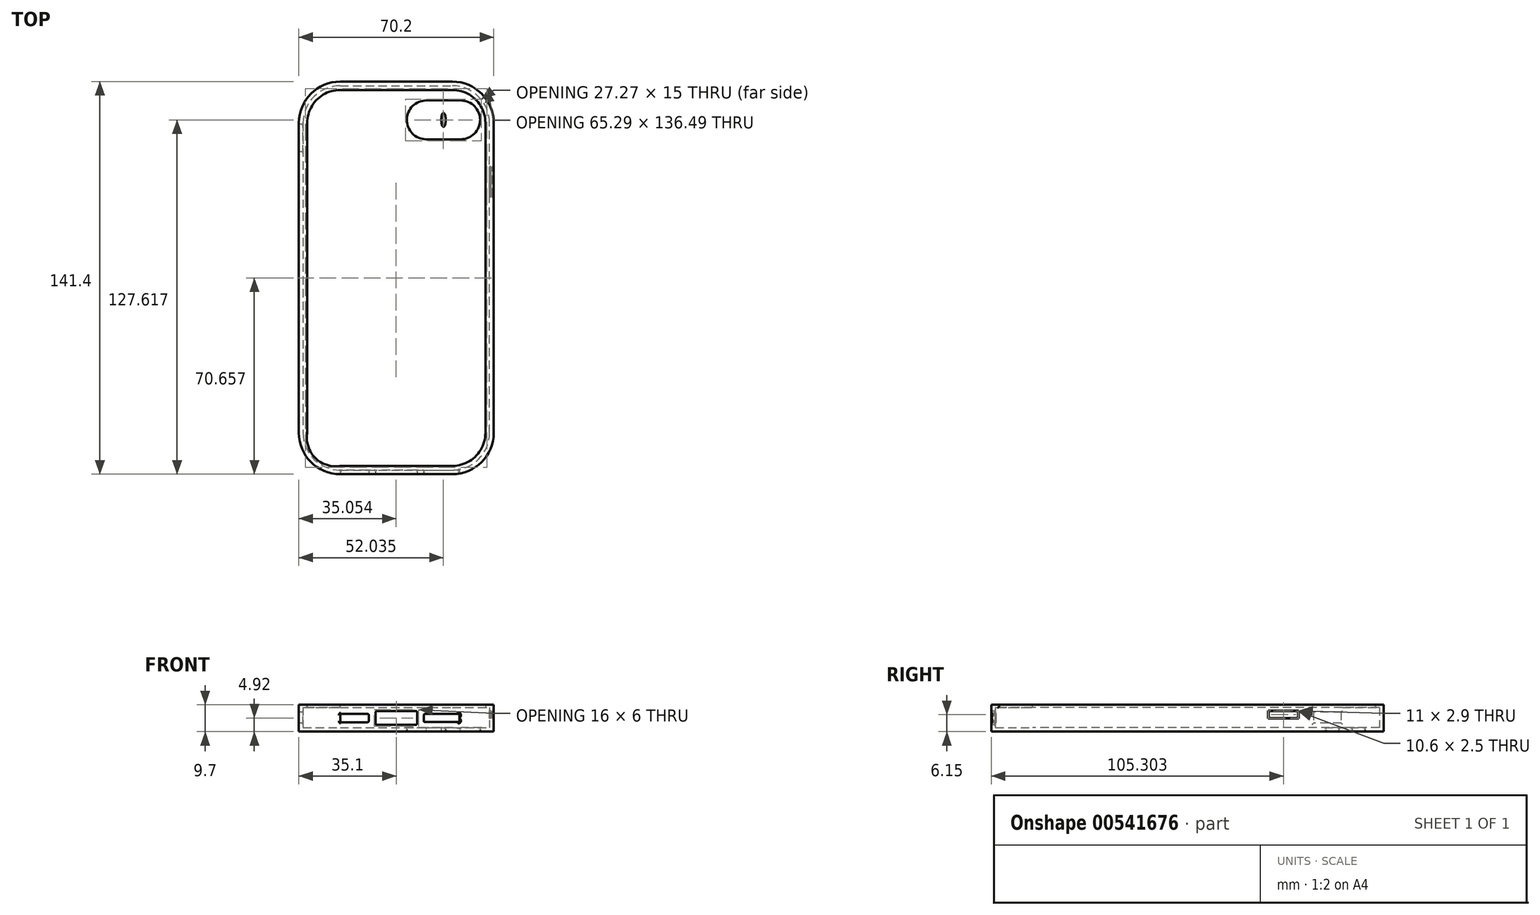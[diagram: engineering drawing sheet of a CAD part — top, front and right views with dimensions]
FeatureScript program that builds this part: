
annotation { "Feature Type Name" : "Feature", "Feature Type Description" : "" }
export const myFeature = defineFeature(function(context is Context, id is Id, definition is map)
    precondition{}
    {
        {
            var Q0;
            Q0=qCreatedBy(makeId("Top.planeOp"),FACE);
            var sketch = newSketch(context, id + "F0", { "sketchPlane" : qUnion([Q0])});
            skArc(sketch, "E0", {"start": v(-23.7, 70.7) * mm, "mid": v(-33.18, 66.77) * mm, "end": v(-37.1, 57.3) * mm});
            skArc(sketch, "E1", {"start": v(-37.1, -54.3) * mm, "mid": v(-33.18, -63.78) * mm, "end": v(-23.7, -67.7) * mm});
            skArc(sketch, "E2", {"start": v(16.7, -67.7) * mm, "mid": v(26.18, -63.78) * mm, "end": v(30.1, -54.3) * mm});
            skArc(sketch, "E3", {"start": v(30.1, 57.3) * mm, "mid": v(26.18, 66.77) * mm, "end": v(16.7, 70.7) * mm});
            skLineSegment(sketch, "E4", {"start": v(-23.7, -67.7) * mm, "end": v(16.7, -67.7) * mm});
            skLineSegment(sketch, "E5", {"start": v(30.1, -54.3) * mm, "end": v(30.1, 57.3) * mm});
            skLineSegment(sketch, "E6", {"start": v(-37.1, 57.3) * mm, "end": v(-37.1, -54.3) * mm});
            skLineSegment(sketch, "E7", {"start": v(-23.7, 70.7) * mm, "end": v(16.7, 70.7) * mm});
            skLineSegment(sketch, "E8.0", {"start": v(-23.7, 72.2) * mm, "end": v(16.7, 72.2) * mm});
            skArc(sketch, "E8.1", {"start": v(31.6, 57.3) * mm, "mid": v(27.24, 67.83) * mm, "end": v(16.7, 72.2) * mm});
            skArc(sketch, "E8.2", {"start": v(-23.7, 72.2) * mm, "mid": v(-34.24, 67.83) * mm, "end": v(-38.6, 57.3) * mm});
            skLineSegment(sketch, "E8.3", {"start": v(31.6, -54.3) * mm, "end": v(31.6, 57.3) * mm});
            skLineSegment(sketch, "E8.4", {"start": v(-38.6, 57.3) * mm, "end": v(-38.6, -54.3) * mm});
            skArc(sketch, "E8.5", {"start": v(-38.6, -54.3) * mm, "mid": v(-34.24, -64.84) * mm, "end": v(-23.7, -69.2) * mm});
            skLineSegment(sketch, "E8.6", {"start": v(-23.7, -69.2) * mm, "end": v(16.7, -69.2) * mm});
            skArc(sketch, "E8.7", {"start": v(16.7, -69.2) * mm, "mid": v(27.24, -64.84) * mm, "end": v(31.6, -54.3) * mm});
            skLineSegment(sketch, "E9", {"start": v(-37.1, -54.3) * mm, "end": v(-3.5, -54.3) * mm, "construction": true});
            skLineSegment(sketch, "E10", {"start": v(-3.5, -54.3) * mm, "end": v(-3.5, -67.7) * mm, "construction": true});
            skSolve(sketch);
        }
        {
            var Q0;
            Q0=makeQuery(id+"F0.imprint","IMPRINT",FACE,{"disambiguationData":[TD([[makeQuery(id+"F0.imprint","IMPRINT",EDGE,{"derivedFrom":sQuery(id+"F0.wireOp",EDGE,"E0")}),-1.0]])]});
            extrude(context, id + "F1", {"entities" : qUnion([Q0]), "depth" : 8.2 * mm, "offsetDistance" : 25 * mm});
        }
        {
            var Q0;
            Q0=makeQuery(id+"F0.imprint","IMPRINT",FACE,{"disambiguationData":[TD([[makeQuery(id+"F0.imprint","IMPRINT",EDGE,{"derivedFrom":sQuery(id+"F0.wireOp",EDGE,"E0")}),1.0]])]});
            var Q1;
            Q1=makeQuery(id+"F0.imprint","IMPRINT",FACE,{"disambiguationData":[TD([[makeQuery(id+"F0.imprint","IMPRINT",EDGE,{"derivedFrom":sQuery(id+"F0.wireOp",EDGE,"E0")}),-1.0]])]});
            extrude(context, id + "F2", {"entities" : qUnion([Q0, Q1]), "operationType" : NewBodyOperationType.ADD, "oppositeDirection" : true, "depth" : 1.5 * mm, "offsetDistance" : 25 * mm});
        }
        {
            var Q0;
            {var subQ0=sQuery(id+"F0.wireOp",EDGE,"E8.6");Q0=makeQuery(id+"F2.boolean.opBoolean","MERGE",FACE,{"derivedFrom":[makeQuery(id+"F1.opExtrude","SWEPT_FACE",FACE,{"disambiguationData":[OSD([subQ0])]}),makeQuery(id+"F2.opExtrude","SWEPT_FACE",FACE,{"disambiguationData":[OSD([subQ0])]})]});}
            var sketch = newSketch(context, id + "F3", { "sketchPlane" : qUnion([Q0])});
            skLineSegment(sketch, "E11", {"start": v(-23.7, 3.42) * mm, "end": v(16.7, 3.42) * mm, "construction": true});
            skLineSegment(sketch, "E12", {"start": v(-3.5, -1.5) * mm, "end": v(-3.5, 8.2) * mm, "construction": true});
            skLineSegment(sketch, "E13.bottom", {"start": v(-11, 5.92) * mm, "end": v(4, 5.92) * mm});
            skLineSegment(sketch, "E13.top", {"start": v(-11, 0.92) * mm, "end": v(4, 0.92) * mm});
            skLineSegment(sketch, "E13.left", {"start": v(-11, 5.92) * mm, "end": v(-11, 0.92) * mm});
            skLineSegment(sketch, "E13.right", {"start": v(4, 5.92) * mm, "end": v(4, 0.92) * mm});
            skPoint(sketch, "E13.middle", {"position": v(-3.5, 3.42) * mm});
            skLineSegment(sketch, "E14.bottom", {"start": v(-23.7, 3.42) * mm, "end": v(-10.9, 3.42) * mm});
            skLineSegment(sketch, "E14.top", {"start": v(-26.2, 4.92) * mm, "end": v(-13.4, 4.92) * mm});
            skLineSegment(sketch, "E14.left", {"start": v(-26.2, 3.42) * mm, "end": v(-26.2, 4.92) * mm});
            skLineSegment(sketch, "E14.right", {"start": v(-13.4, 3.42) * mm, "end": v(-13.4, 4.92) * mm});
            skLineSegment(sketch, "E15.top", {"start": v(-26.2, 1.87) * mm, "end": v(-13.4, 1.87) * mm});
            skLineSegment(sketch, "E15.left", {"start": v(-26.2, 3.42) * mm, "end": v(-26.2, 1.87) * mm});
            skLineSegment(sketch, "E15.right", {"start": v(-13.4, 3.42) * mm, "end": v(-13.4, 1.87) * mm});
            skLineSegment(sketch, "E16.bottom", {"start": v(19.2, 3.42) * mm, "end": v(6.4, 3.42) * mm});
            skLineSegment(sketch, "E16.top", {"start": v(19.2, 4.92) * mm, "end": v(6.4, 4.92) * mm});
            skLineSegment(sketch, "E16.left", {"start": v(19.2, 3.42) * mm, "end": v(19.2, 4.92) * mm});
            skLineSegment(sketch, "E16.right", {"start": v(6.4, 3.42) * mm, "end": v(6.4, 4.92) * mm});
            skLineSegment(sketch, "E17.top", {"start": v(19.2, 1.92) * mm, "end": v(6.4, 1.92) * mm});
            skLineSegment(sketch, "E17.left", {"start": v(19.2, 3.42) * mm, "end": v(19.2, 1.92) * mm});
            skLineSegment(sketch, "E17.right", {"start": v(6.4, 3.42) * mm, "end": v(6.4, 1.92) * mm});
            skSolve(sketch);
        }
        {
            var Q0;
            Q0=makeQuery(id+"F3.imprint","IMPRINT",FACE,{"disambiguationData":[TD([[makeQuery(id+"F3.imprint","IMPRINT",EDGE,{"derivedFrom":sQuery(id+"F3.wireOp",EDGE,"E14.bottom")}),-1.0]])]});
            var Q1;
            Q1=makeQuery(id+"F3.imprint","IMPRINT",FACE,{"disambiguationData":[TD([[makeQuery(id+"F3.imprint","IMPRINT",EDGE,{"derivedFrom":sQuery(id+"F3.wireOp",EDGE,"E14.top")}),-1.0]])]});
            var Q2;
            Q2=makeQuery(id+"F3.imprint","IMPRINT",FACE,{"disambiguationData":[TD([[makeQuery(id+"F3.imprint","IMPRINT",EDGE,{"derivedFrom":sQuery(id+"F3.wireOp",EDGE,"E13.bottom")}),-1.0]])]});
            var Q3;
            Q3=makeQuery(id+"F3.imprint","IMPRINT",FACE,{"disambiguationData":[TD([[makeQuery(id+"F3.imprint","IMPRINT",EDGE,{"derivedFrom":sQuery(id+"F3.wireOp",EDGE,"E16.top")}),1.0]])]});
            var Q4;
            Q4=makeQuery(id+"F3.imprint","IMPRINT",FACE,{"disambiguationData":[TD([[makeQuery(id+"F3.imprint","IMPRINT",EDGE,{"derivedFrom":sQuery(id+"F3.wireOp",EDGE,"E16.bottom")}),1.0]])]});
            extrude(context, id + "F4", {"entities" : qUnion([Q0, Q1, Q2, Q3, Q4]), "operationType" : NewBodyOperationType.REMOVE, "oppositeDirection" : true, "depth" : 3 * mm, "offsetDistance" : 25 * mm});
        }
        {
            var Q0;
            Q0=makeQuery(id+"F2.opExtrude","CAP_FACE",FACE,{"disambiguationData":[OSD([sQuery(id+"F0.wireOp",EDGE,"E8.0"),sQuery(id+"F0.wireOp",EDGE,"E8.1"),sQuery(id+"F0.wireOp",EDGE,"E8.2"),sQuery(id+"F0.wireOp",EDGE,"E8.3"),sQuery(id+"F0.wireOp",EDGE,"E8.4"),sQuery(id+"F0.wireOp",EDGE,"E8.5"),sQuery(id+"F0.wireOp",EDGE,"E8.6"),sQuery(id+"F0.wireOp",EDGE,"E8.7")])],"isStart":false});
            var sketch = newSketch(context, id + "F5", { "sketchPlane" : qUnion([Q0])});
            skCircle(sketch, "E18", {"center": v(19.7, -58.4) * mm, "radius": 7 * mm});
            skCircle(sketch, "E19.1.0.0", {"center": v(7.3, -58.4) * mm, "radius": 7 * mm});
            skLineSegment(sketch, "E19.direction1", {"start": v(19.7, -58.4) * mm, "end": v(7.3, -58.4) * mm, "construction": true});
            skLineSegment(sketch, "E20", {"start": v(19.75, -65.4) * mm, "end": v(7.3, -65.4) * mm});
            skLineSegment(sketch, "E21", {"start": v(7.2, -51.4) * mm, "end": v(19.7, -51.4) * mm});
            skSolve(sketch);
        }
        {
            var Q0;
            {var subQ0=sQuery(id+"F5.wireOp",EDGE,"E18");var subQ3=makeQuery(id+"F5.imprint","IMPRINT",VERTEX,{"derivedFrom":subQ0});Q0=makeQuery(id+"F5.imprint","IMPRINT",FACE,{"disambiguationData":[TD([[makeQuery(id+"F5.imprint","IMPRINT",EDGE,{"disambiguationData":[TD([[subQ3,1.0]])],"derivedFrom":subQ0}),1.0]])]});}
            var Q1;
            {var subQ0=sQuery(id+"F5.wireOp",EDGE,"E19.1.0.0");var subQ1=makeQuery(id+"F5.imprint","INTERSECT",VERTEX,{"derivedFrom":[subQ0,sQuery(id+"F5.wireOp",EDGE,"E20")]});Q1=makeQuery(id+"F5.imprint","IMPRINT",FACE,{"disambiguationData":[TD([[makeQuery(id+"F5.imprint","IMPRINT",EDGE,{"disambiguationData":[TD([[subQ1,1.0]])],"derivedFrom":subQ0}),1.0]])]});}
            var Q2;
            {var subQ0=sQuery(id+"F5.wireOp",EDGE,"E20");Q2=makeQuery(id+"F5.imprint","IMPRINT",FACE,{"disambiguationData":[TD([[makeQuery(id+"F5.imprint","IMPRINT",EDGE,{"derivedFrom":subQ0}),-1.0]])]});}
            var Q3;
            {var subQ0=sQuery(id+"F5.wireOp",EDGE,"E19.1.0.0");var subQ1=sQuery(id+"F5.wireOp",EDGE,"E18");var subQ2=makeQuery(id+"F5.imprint","INTERSECT",VERTEX,{"disambiguationData":[OD(0.0)],"derivedFrom":[subQ1,subQ0]});Q3=makeQuery(id+"F5.imprint","IMPRINT",FACE,{"disambiguationData":[TD([[makeQuery(id+"F5.imprint","IMPRINT",EDGE,{"disambiguationData":[TD([[subQ2,-1.0]])],"derivedFrom":subQ1}),1.0]])]});}
            var Q4;
            {var subQ0=sQuery(id+"F5.wireOp",EDGE,"E21");var subQ1=sQuery(id+"F5.wireOp",EDGE,"E18");var subQ2=makeQuery(id+"F5.imprint","INTERSECT",VERTEX,{"derivedFrom":[subQ1,subQ0]});Q4=makeQuery(id+"F5.imprint","IMPRINT",FACE,{"disambiguationData":[TD([[makeQuery(id+"F5.imprint","IMPRINT",EDGE,{"disambiguationData":[TD([[subQ2,-1.0]])],"derivedFrom":subQ1}),-1.0]])]});}
            extrude(context, id + "F6", {"entities" : qUnion([Q0, Q1, Q2, Q3, Q4]), "operationType" : NewBodyOperationType.REMOVE, "oppositeDirection" : true, "depth" : 5 * mm, "offsetDistance" : 25 * mm});
        }
        {
            var Q0;
            Q0=makeQuery(id+"F1.opExtrude","SWEPT_FACE",FACE,{"disambiguationData":[OSD([sQuery(id+"F0.wireOp",EDGE,"E5")])]});
            var sketch = newSketch(context, id + "F7", { "sketchPlane" : qUnion([Q0])});
            skLineSegment(sketch, "E22", {"start": v(-57.3, 4.65) * mm, "end": v(-33.08, 4.65) * mm, "construction": true});
            skLineSegment(sketch, "E23", {"start": v(-36.1, 8.2) * mm, "end": v(-36.1, 0) * mm, "construction": true});
            skLineSegment(sketch, "E24.bottom", {"start": v(-36.1, 4.65) * mm, "end": v(-41.4, 4.65) * mm});
            skLineSegment(sketch, "E24.top", {"start": v(-36.1, 5.9) * mm, "end": v(-41.4, 5.9) * mm});
            skLineSegment(sketch, "E24.left", {"start": v(-36.1, 4.65) * mm, "end": v(-36.1, 5.9) * mm});
            skLineSegment(sketch, "E24.right", {"start": v(-41.4, 4.65) * mm, "end": v(-41.4, 5.9) * mm});
            skLineSegment(sketch, "E25.top", {"start": v(-36.1, 3.4) * mm, "end": v(-41.4, 3.4) * mm});
            skLineSegment(sketch, "E25.left", {"start": v(-36.1, 4.65) * mm, "end": v(-36.1, 3.4) * mm});
            skLineSegment(sketch, "E25.right", {"start": v(-41.4, 4.65) * mm, "end": v(-41.4, 3.4) * mm});
            skLineSegment(sketch, "E26.bottom", {"start": v(-41.4, 5.9) * mm, "end": v(-30.8, 5.9) * mm});
            skLineSegment(sketch, "E26.top", {"start": v(-41.4, 3.4) * mm, "end": v(-30.8, 3.4) * mm});
            skLineSegment(sketch, "E26.right", {"start": v(-30.8, 5.9) * mm, "end": v(-30.8, 3.4) * mm});
            skPoint(sketch, "E26.middle", {"position": v(-36.1, 4.65) * mm});
            skLineSegment(sketch, "E27.0", {"start": v(-41.6, 6.1) * mm, "end": v(-30.6, 6.1) * mm});
            skLineSegment(sketch, "E27.1", {"start": v(-41.6, 4.65) * mm, "end": v(-41.6, 6.1) * mm});
            skLineSegment(sketch, "E27.2", {"start": v(-30.6, 6.1) * mm, "end": v(-30.6, 3.2) * mm});
            skLineSegment(sketch, "E27.3", {"start": v(-41.6, 3.2) * mm, "end": v(-30.6, 3.2) * mm});
            skLineSegment(sketch, "E27.4", {"start": v(-41.6, 4.65) * mm, "end": v(-41.6, 3.2) * mm});
            skSolve(sketch);
        }
        {
            var Q0;
            {var subQ4=sQuery(id+"F7.wireOp",EDGE,"E24.right");Q0=makeQuery(id+"F7.imprint","IMPRINT",FACE,{"disambiguationData":[TD([[makeQuery(id+"F7.imprint","IMPRINT",EDGE,{"derivedFrom":subQ4}),1.0]])]});}
            extrude(context, id + "F8", {"entities" : qUnion([Q0]), "operationType" : NewBodyOperationType.REMOVE, "oppositeDirection" : true, "depth" : .5 * mm, "offsetDistance" : 25 * mm});
        }
        {
            var Q0;
            {var subQ0=sQuery(id+"F0.wireOp",EDGE,"E8.3");Q0=makeQuery(id+"F2.boolean.opBoolean","MERGE",FACE,{"derivedFrom":[makeQuery(id+"F1.opExtrude","SWEPT_FACE",FACE,{"disambiguationData":[OSD([subQ0])]}),makeQuery(id+"F2.opExtrude","SWEPT_FACE",FACE,{"disambiguationData":[OSD([subQ0])]})]});}
            var sketch = newSketch(context, id + "F9", { "sketchPlane" : qUnion([Q0])});
            skLineSegment(sketch, "E28.bottom", {"start": v(30.8, 5.9) * mm, "end": v(41.4, 5.9) * mm});
            skLineSegment(sketch, "E28.top", {"start": v(30.8, 3.4) * mm, "end": v(41.4, 3.4) * mm});
            skLineSegment(sketch, "E28.right", {"start": v(41.4, 5.9) * mm, "end": v(41.4, 3.4) * mm});
            skLineSegment(sketch, "E29", {"start": v(30.8, 5.9) * mm, "end": v(30.8, 3.4) * mm});
            skLineSegment(sketch, "E30.0", {"start": v(41.6, 6.1) * mm, "end": v(41.6, 3.2) * mm});
            skLineSegment(sketch, "E30.1", {"start": v(30.6, 6.1) * mm, "end": v(41.6, 6.1) * mm});
            skLineSegment(sketch, "E30.2", {"start": v(30.6, 6.1) * mm, "end": v(30.6, 3.2) * mm});
            skLineSegment(sketch, "E30.3", {"start": v(30.6, 3.2) * mm, "end": v(41.6, 3.2) * mm});
            skLineSegment(sketch, "E31.0", {"start": v(-59.3, 13.2) * mm, "end": v(-59.3, -6.5) * mm});
            skLineSegment(sketch, "E31.1", {"start": v(62.3, 13.2) * mm, "end": v(-59.3, 13.2) * mm});
            skLineSegment(sketch, "E31.2", {"start": v(62.3, -6.5) * mm, "end": v(62.3, 13.2) * mm});
            skLineSegment(sketch, "E31.3", {"start": v(-59.3, -6.5) * mm, "end": v(62.3, -6.5) * mm});
            skSolve(sketch);
        }
        {
            var Q0;
            Q0=makeQuery(id+"F9.imprint","IMPRINT",FACE,{"disambiguationData":[TD([[makeQuery(id+"F9.imprint","IMPRINT",EDGE,{"derivedFrom":sQuery(id+"F9.wireOp",EDGE,"E28.bottom")}),1.0]])]});
            extrude(context, id + "F10", {"entities" : qUnion([Q0]), "operationType" : NewBodyOperationType.REMOVE, "oppositeDirection" : true, "depth" : .5 * mm, "offsetDistance" : 25 * mm});
        }
        {
            var Q0;
            {var subQ0=sQuery(id+"F0.wireOp",EDGE,"E8.4");Q0=makeQuery(id+"F2.boolean.opBoolean","MERGE",FACE,{"derivedFrom":[makeQuery(id+"F1.opExtrude","SWEPT_FACE",FACE,{"disambiguationData":[OSD([subQ0])]}),makeQuery(id+"F2.opExtrude","SWEPT_FACE",FACE,{"disambiguationData":[OSD([subQ0])]})]});}
            var sketch = newSketch(context, id + "F11", { "sketchPlane" : qUnion([Q0])});
            skLineSegment(sketch, "E32", {"start": v(-68.46, 3.55) * mm, "end": v(5.63, 3.55) * mm, "construction": true});
            skLineSegment(sketch, "E33", {"start": v(-56.9, 8.2) * mm, "end": v(-56.9, 0) * mm, "construction": true});
            skLineSegment(sketch, "E34.bottom", {"start": v(-56.9, 3.55) * mm, "end": v(-46.9, 3.55) * mm});
            skLineSegment(sketch, "E34.top", {"start": v(-56.9, 5.55) * mm, "end": v(-46.9, 5.55) * mm});
            skLineSegment(sketch, "E34.left", {"start": v(-56.9, 3.55) * mm, "end": v(-56.9, 5.55) * mm});
            skLineSegment(sketch, "E34.right", {"start": v(-46.9, 3.55) * mm, "end": v(-46.9, 5.55) * mm});
            skLineSegment(sketch, "E35.top", {"start": v(-56.9, 1.55) * mm, "end": v(-46.9, 1.55) * mm});
            skLineSegment(sketch, "E35.left", {"start": v(-56.9, 5.55) * mm, "end": v(-56.9, 1.55) * mm});
            skLineSegment(sketch, "E35.right", {"start": v(-46.9, 5.55) * mm, "end": v(-46.9, 1.55) * mm});
            skSolve(sketch);
        }
        {
            var Q0;
            {var subQ0=sQuery(id+"F11.wireOp",EDGE,"E34.bottom");Q0=makeQuery(id+"F11.imprint","IMPRINT",FACE,{"disambiguationData":[TD([[makeQuery(id+"F11.imprint","IMPRINT",EDGE,{"derivedFrom":subQ0}),-1.0]])]});}
            var Q1;
            {var subQ0=sQuery(id+"F11.wireOp",EDGE,"E34.bottom");Q1=makeQuery(id+"F11.imprint","IMPRINT",FACE,{"disambiguationData":[TD([[makeQuery(id+"F11.imprint","IMPRINT",EDGE,{"derivedFrom":subQ0}),1.0]])]});}
            extrude(context, id + "F12", {"entities" : qUnion([Q0, Q1]), "operationType" : NewBodyOperationType.REMOVE, "oppositeDirection" : true, "depth" : 5 * mm, "offsetDistance" : 25 * mm});
        }
        {
            var Q0;
            Q0=makeQuery(id+"F1.opExtrude","CAP_FACE",FACE,{"disambiguationData":[OSD([sQuery(id+"F0.wireOp",EDGE,"E0"),sQuery(id+"F0.wireOp",EDGE,"E1"),sQuery(id+"F0.wireOp",EDGE,"E2"),sQuery(id+"F0.wireOp",EDGE,"E3"),sQuery(id+"F0.wireOp",EDGE,"E4"),sQuery(id+"F0.wireOp",EDGE,"E5"),sQuery(id+"F0.wireOp",EDGE,"E6"),sQuery(id+"F0.wireOp",EDGE,"E7"),sQuery(id+"F0.wireOp",EDGE,"E8.0"),sQuery(id+"F0.wireOp",EDGE,"E8.1"),sQuery(id+"F0.wireOp",EDGE,"E8.2"),sQuery(id+"F0.wireOp",EDGE,"E8.3"),sQuery(id+"F0.wireOp",EDGE,"E8.4"),sQuery(id+"F0.wireOp",EDGE,"E8.5"),sQuery(id+"F0.wireOp",EDGE,"E8.6"),sQuery(id+"F0.wireOp",EDGE,"E8.7")])],"isStart":false});
            var sketch = newSketch(context, id + "F13", { "sketchPlane" : qUnion([Q0])});
            skArc(sketch, "E36", {"start": v(-23.7, 70.7) * mm, "mid": v(-33.18, 66.77) * mm, "end": v(-37.1, 57.3) * mm});
            skArc(sketch, "E37", {"start": v(-37.1, -54.3) * mm, "mid": v(-33.77, -64.38) * mm, "end": v(-23.7, -67.7) * mm});
            skArc(sketch, "E38", {"start": v(16.7, -67.7) * mm, "mid": v(26.18, -63.78) * mm, "end": v(30.1, -54.3) * mm});
            skArc(sketch, "E39", {"start": v(30.1, 57.3) * mm, "mid": v(26.18, 66.77) * mm, "end": v(16.7, 70.7) * mm});
            skLineSegment(sketch, "E40", {"start": v(-23.7, -67.7) * mm, "end": v(16.7, -67.7) * mm});
            skLineSegment(sketch, "E41", {"start": v(30.1, -54.3) * mm, "end": v(30.1, 57.3) * mm});
            skLineSegment(sketch, "E42", {"start": v(-37.1, 57.3) * mm, "end": v(-37.1, -54.3) * mm});
            skLineSegment(sketch, "E43", {"start": v(-23.7, 70.7) * mm, "end": v(16.7, 70.7) * mm});
            skLineSegment(sketch, "E44", {"start": v(-37.1, -54.3) * mm, "end": v(-3.5, -54.3) * mm, "construction": true});
            skLineSegment(sketch, "E45", {"start": v(-3.5, -54.3) * mm, "end": v(-3.5, -67.7) * mm, "construction": true});
            skArc(sketch, "E46.0", {"start": v(16.7, -66.2) * mm, "mid": v(25.11, -62.72) * mm, "end": v(28.6, -54.3) * mm});
            skLineSegment(sketch, "E46.1", {"start": v(-23.81, -66.2) * mm, "end": v(16.7, -66.2) * mm});
            skLineSegment(sketch, "E46.2", {"start": v(28.6, -54.3) * mm, "end": v(28.6, 57.3) * mm});
            skArc(sketch, "E46.3", {"start": v(-35.6, -54.42) * mm, "mid": v(-32.71, -63.32) * mm, "end": v(-23.81, -66.2) * mm});
            skArc(sketch, "E46.4", {"start": v(28.6, 57.3) * mm, "mid": v(25.11, 65.7) * mm, "end": v(16.7, 69.2) * mm});
            skLineSegment(sketch, "E46.5", {"start": v(-23.7, 69.2) * mm, "end": v(16.7, 69.2) * mm});
            skArc(sketch, "E46.6", {"start": v(-23.7, 69.2) * mm, "mid": v(-32.11, 65.7) * mm, "end": v(-35.6, 57.3) * mm});
            skLineSegment(sketch, "E46.7", {"start": v(-35.6, 57.3) * mm, "end": v(-35.6, -54.42) * mm});
            skSolve(sketch);
        }
        {
            var Q0;
            Q0=makeQuery(id+"F13.imprint","IMPRINT",FACE,{"disambiguationData":[TD([[makeQuery(id+"F13.imprint","IMPRINT",EDGE,{"derivedFrom":sQuery(id+"F13.wireOp",EDGE,"E36")}),1.0]])]});
            extrude(context, id + "F14", {"entities" : qUnion([Q0]), "operationType" : NewBodyOperationType.ADD, "oppositeDirection" : true, "depth" : 1 * mm, "offsetDistance" : 25 * mm});
        }
        {
            var Q0;
            Q0=makeQuery(id+"F14.opExtrude","CAP_EDGE",EDGE,{"disambiguationData":[OSD([sQuery(id+"F13.wireOp",EDGE,"E46.7")])],"isStart":true});
            var Q1;
            Q1=makeQuery(id+"F14.opExtrude","CAP_EDGE",EDGE,{"disambiguationData":[OSD([sQuery(id+"F13.wireOp",EDGE,"E46.7")])],"isStart":false});
            var Q2;
            Q2=makeQuery(id+"F14.opExtrude","CAP_EDGE",EDGE,{"disambiguationData":[OSD([sQuery(id+"F13.wireOp",EDGE,"E46.3")])],"isStart":true});
            var Q3;
            Q3=makeQuery(id+"F14.opExtrude","CAP_EDGE",EDGE,{"disambiguationData":[OSD([sQuery(id+"F13.wireOp",EDGE,"E46.3")])],"isStart":false});
            var Q4;
            Q4=makeQuery(id+"F6.boolean.opBoolean","COPY",FACE,{"derivedFrom":makeQuery(id+"F6.opExtrude","SWEPT_FACE",FACE,{"disambiguationData":[OSD([sQuery(id+"F5.wireOp",EDGE,"E19.1.0.0")])]})});
            var Q5;
            Q5=makeQuery(id+"F12.boolean.opBoolean","COPY",EDGE,{"derivedFrom":makeQuery(id+"F12.opExtrude","CAP_EDGE",EDGE,{"disambiguationData":[OSD([sQuery(id+"F11.wireOp",EDGE,"E35.top")])],"isStart":true})});
            var Q6;
            Q6=makeQuery(id+"F12.boolean.opBoolean","INTERSECT",EDGE,{"derivedFrom":[makeQuery(id+"F1.opExtrude","SWEPT_FACE",FACE,{"disambiguationData":[OSD([sQuery(id+"F0.wireOp",EDGE,"E6")])]}),makeQuery(id+"F12.opExtrude","SWEPT_FACE",FACE,{"disambiguationData":[OSD([sQuery(id+"F11.wireOp",EDGE,"E35.top")])]})]});
            var Q7;
            Q7=makeQuery(id+"F12.boolean.opBoolean","COPY",EDGE,{"derivedFrom":makeQuery(id+"F12.opExtrude","CAP_EDGE",EDGE,{"disambiguationData":[OSD([sQuery(id+"F11.wireOp",EDGE,"E35.right")])],"isStart":true})});
            var Q8;
            Q8=makeQuery(id+"F12.boolean.opBoolean","INTERSECT",EDGE,{"derivedFrom":[makeQuery(id+"F1.opExtrude","SWEPT_FACE",FACE,{"disambiguationData":[OSD([sQuery(id+"F0.wireOp",EDGE,"E6")])]}),makeQuery(id+"F12.opExtrude","SWEPT_FACE",FACE,{"disambiguationData":[OSD([sQuery(id+"F11.wireOp",EDGE,"E35.right")])]})]});
            var Q9;
            Q9=makeQuery(id+"F12.boolean.opBoolean","INTERSECT",EDGE,{"derivedFrom":[makeQuery(id+"F1.opExtrude","SWEPT_FACE",FACE,{"disambiguationData":[OSD([sQuery(id+"F0.wireOp",EDGE,"E6")])]}),makeQuery(id+"F12.opExtrude","SWEPT_FACE",FACE,{"disambiguationData":[OSD([sQuery(id+"F11.wireOp",EDGE,"E35.left")])]})]});
            var Q10;
            Q10=makeQuery(id+"F12.boolean.opBoolean","COPY",EDGE,{"derivedFrom":makeQuery(id+"F12.opExtrude","CAP_EDGE",EDGE,{"disambiguationData":[OSD([sQuery(id+"F11.wireOp",EDGE,"E35.left")])],"isStart":true})});
            var Q11;
            Q11=makeQuery(id+"F12.boolean.opBoolean","INTERSECT",EDGE,{"derivedFrom":[makeQuery(id+"F1.opExtrude","SWEPT_FACE",FACE,{"disambiguationData":[OSD([sQuery(id+"F0.wireOp",EDGE,"E6")])]}),makeQuery(id+"F12.opExtrude","SWEPT_FACE",FACE,{"disambiguationData":[OSD([sQuery(id+"F11.wireOp",EDGE,"E34.top")])]})]});
            var Q12;
            Q12=makeQuery(id+"F12.boolean.opBoolean","COPY",EDGE,{"derivedFrom":makeQuery(id+"F12.opExtrude","CAP_EDGE",EDGE,{"disambiguationData":[OSD([sQuery(id+"F11.wireOp",EDGE,"E34.top")])],"isStart":true})});
            var Q13;
            Q13=makeQuery(id+"F4.boolean.opBoolean","COPY",FACE,{"derivedFrom":makeQuery(id+"F4.opExtrude","SWEPT_FACE",FACE,{"disambiguationData":[OSD([sQuery(id+"F3.wireOp",EDGE,"E13.top")])]})});
            var Q14;
            Q14=makeQuery(id+"F4.boolean.opBoolean","COPY",FACE,{"derivedFrom":makeQuery(id+"F4.opExtrude","SWEPT_FACE",FACE,{"disambiguationData":[OSD([sQuery(id+"F3.wireOp",EDGE,"E13.bottom")])]})});
            var Q15;
            Q15=makeQuery(id+"F4.boolean.opBoolean","COPY",FACE,{"derivedFrom":makeQuery(id+"F4.opExtrude","SWEPT_FACE",FACE,{"disambiguationData":[OSD([sQuery(id+"F0.wireOp",EDGE,"E8.5"),sQuery(id+"F0.wireOp",EDGE,"E8.6")])]})});
            var Q16;
            Q16=makeQuery(id+"F4.boolean.opBoolean","COPY",FACE,{"derivedFrom":makeQuery(id+"F4.opExtrude","SWEPT_FACE",FACE,{"disambiguationData":[OSD([sQuery(id+"F3.wireOp",EDGE,"E14.top")])]})});
            var Q17;
            Q17=makeQuery(id+"F4.boolean.opBoolean","COPY",FACE,{"derivedFrom":makeQuery(id+"F4.opExtrude","SWEPT_FACE",FACE,{"disambiguationData":[OSD([sQuery(id+"F3.wireOp",EDGE,"E14.right"),sQuery(id+"F3.wireOp",EDGE,"E15.right")])]})});
            var Q18;
            Q18=makeQuery(id+"F4.boolean.opBoolean","COPY",FACE,{"derivedFrom":makeQuery(id+"F4.opExtrude","SWEPT_FACE",FACE,{"disambiguationData":[OSD([sQuery(id+"F3.wireOp",EDGE,"E15.top")])]})});
            var Q19;
            Q19=makeQuery(id+"F4.boolean.opBoolean","COPY",FACE,{"derivedFrom":makeQuery(id+"F4.opExtrude","SWEPT_FACE",FACE,{"disambiguationData":[OSD([sQuery(id+"F3.wireOp",EDGE,"E17.top")])]})});
            var Q20;
            Q20=makeQuery(id+"F4.boolean.opBoolean","COPY",FACE,{"derivedFrom":makeQuery(id+"F4.opExtrude","SWEPT_FACE",FACE,{"disambiguationData":[OSD([sQuery(id+"F3.wireOp",EDGE,"E16.top")])]})});
            fillet(context, id + "F15", {"entities" : qUnion([Q0, Q1, Q2, Q3, Q4, Q5, Q6, Q7, Q8, Q9, Q10, Q11, Q12, Q13, Q14, Q15, Q16, Q17, Q18, Q19, Q20]), "radius" : .5 * mm, "tangentPropagation" : true, "allowEdgeOverflow" : false});
        }
    });
